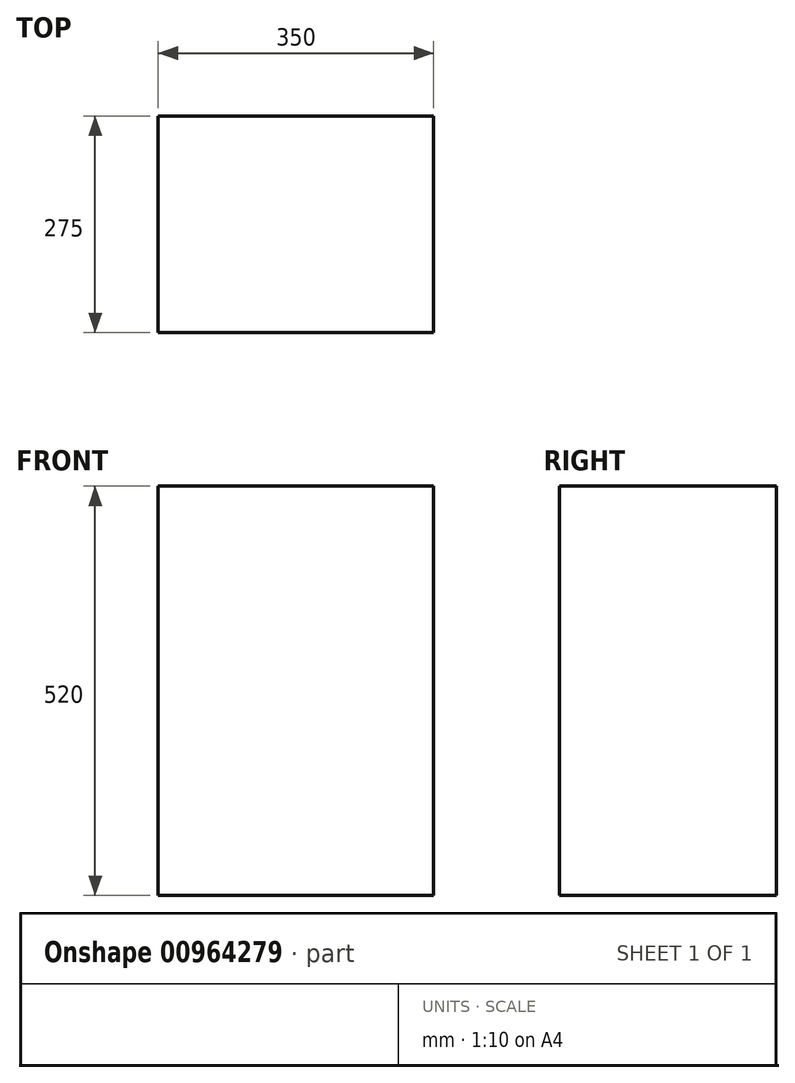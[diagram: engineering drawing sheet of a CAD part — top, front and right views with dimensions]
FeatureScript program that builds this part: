
annotation { "Feature Type Name" : "Feature", "Feature Type Description" : "" }
export const myFeature = defineFeature(function(context is Context, id is Id, definition is map)
    precondition{}
    {
        {
            var Q0;
            Q0=qCreatedBy(makeId("Front.planeOp"),FACE);
            var sketch = newSketch(context, id + "F0", { "sketchPlane" : qUnion([Q0])});
            skLineSegment(sketch, "E0.bottom", {"start": v(-175, 0) * mm, "end": v(175, 0) * mm});
            skLineSegment(sketch, "E0.top", {"start": v(-175, 520) * mm, "end": v(175, 520) * mm});
            skLineSegment(sketch, "E0.left", {"start": v(-175, 0) * mm, "end": v(-175, 520) * mm});
            skLineSegment(sketch, "E0.right", {"start": v(175, 0) * mm, "end": v(175, 520) * mm});
            skSolve(sketch);
        }
        {
            var Q0;
            Q0 = qSketchRegion(id + "F0", true);
            extrude(context, id + "F1", {"entities" : qUnion([Q0]), "depth" : 275 * mm, "offsetDistance" : 25 * mm});
        }
    });
